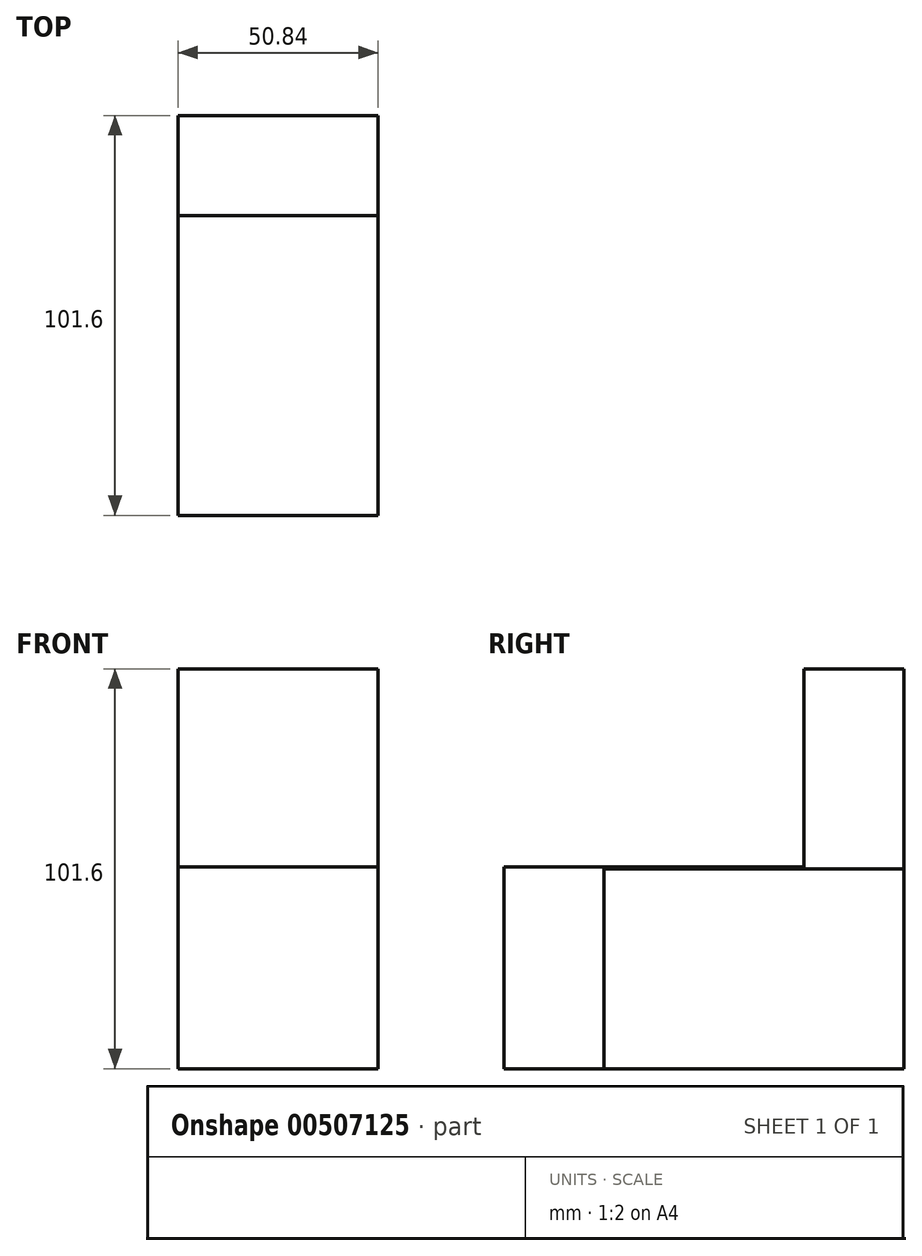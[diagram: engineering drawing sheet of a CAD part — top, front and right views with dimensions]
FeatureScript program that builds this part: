
annotation { "Feature Type Name" : "Feature", "Feature Type Description" : "" }
export const myFeature = defineFeature(function(context is Context, id is Id, definition is map)
    precondition{}
    {
        {
            var Q0;
            Q0=qCreatedBy(makeId("Front.planeOp"),FACE);
            var sketch = newSketch(context, id + "F0", { "sketchPlane" : qUnion([Q0])});
            skLineSegment(sketch, "E0.bottom", {"start": v(-98.06, -18.13) * mm, "end": v(-47.26, -18.13) * mm});
            skLineSegment(sketch, "E0.top", {"start": v(-98.06, -119.73) * mm, "end": v(105.14, -119.73) * mm});
            skLineSegment(sketch, "E0.left", {"start": v(-98.06, -18.13) * mm, "end": v(-98.06, -119.73) * mm});
            skLineSegment(sketch, "E0.right", {"start": v(105.14, -68.93) * mm, "end": v(105.14, -119.73) * mm});
            skLineSegment(sketch, "E1.top", {"start": v(105.14, -68.93) * mm, "end": v(-47.26, -68.93) * mm});
            skLineSegment(sketch, "E1.right", {"start": v(-47.26, -18.13) * mm, "end": v(-47.26, -68.93) * mm});
            skLineSegment(sketch, "E2.bottom", {"start": v(105.14, -68.93) * mm, "end": v(-47.22, -68.93) * mm});
            skLineSegment(sketch, "E2.top", {"start": v(105.14, -119.73) * mm, "end": v(-47.22, -119.73) * mm});
            skLineSegment(sketch, "E2.right", {"start": v(-47.22, -68.93) * mm, "end": v(-47.22, -119.73) * mm});
            skSolve(sketch);
        }
        {
            var Q0;
            Q0=makeQuery(id+"F0.imprint","IMPRINT",FACE,{"disambiguationData":[TD([[makeQuery(id+"F0.imprint","IMPRINT",EDGE,{"derivedFrom":sQuery(id+"F0.wireOp",EDGE,"E0.bottom")}),-1.0]])]});
            var Q1;
            Q1=makeQuery(id+"F0.imprint","IMPRINT",FACE,{"disambiguationData":[TD([[makeQuery(id+"F0.imprint","IMPRINT",EDGE,{"derivedFrom":sQuery(id+"F0.wireOp",EDGE,"E2.bottom")}),1.0]])]});
            extrude(context, id + "F1", {"entities" : qUnion([Q0, Q1]), "oppositeDirection" : true, "depth" : 101.6 * mm});
        }
        {
            var Q0;
            Q0=qCreatedBy(makeId("Front.planeOp"),FACE);
            var sketch = newSketch(context, id + "F2", { "sketchPlane" : qUnion([Q0])});
            skLineSegment(sketch, "E3.bottom", {"start": v(105.14, -68.93) * mm, "end": v(-47.26, -68.93) * mm});
            skLineSegment(sketch, "E3.top", {"start": v(105.14, -119.73) * mm, "end": v(-47.26, -119.73) * mm});
            skLineSegment(sketch, "E3.left", {"start": v(105.14, -68.93) * mm, "end": v(105.14, -119.73) * mm});
            skLineSegment(sketch, "E3.right", {"start": v(-47.26, -68.93) * mm, "end": v(-47.26, -119.73) * mm});
            skSolve(sketch);
        }
        {
            var Q0;
            Q0 = qSketchRegion(id + "F2", true);
            extrude(context, id + "F3", {"entities" : qUnion([Q0]), "operationType" : NewBodyOperationType.REMOVE, "oppositeDirection" : true, "depth" : 25.4 * mm});
        }
        {
            var Q0;
            Q0=qCreatedBy(makeId("Front.planeOp"),FACE);
            var sketch = newSketch(context, id + "F4", { "sketchPlane" : qUnion([Q0])});
            skLineSegment(sketch, "E4.bottom", {"start": v(-47.26, -17.69) * mm, "end": v(-98.06, -17.69) * mm});
            skLineSegment(sketch, "E4.top", {"start": v(-47.26, -68.49) * mm, "end": v(-98.06, -68.49) * mm});
            skLineSegment(sketch, "E4.left", {"start": v(-47.26, -17.69) * mm, "end": v(-47.26, -68.49) * mm});
            skLineSegment(sketch, "E4.right", {"start": v(-98.06, -17.69) * mm, "end": v(-98.06, -68.49) * mm});
            skSolve(sketch);
        }
        {
            var Q0;
            Q0 = qSketchRegion(id + "F4", true);
            extrude(context, id + "F5", {"entities" : qUnion([Q0]), "operationType" : NewBodyOperationType.REMOVE, "oppositeDirection" : true, "depth" : 76.2 * mm});
        }
    });
